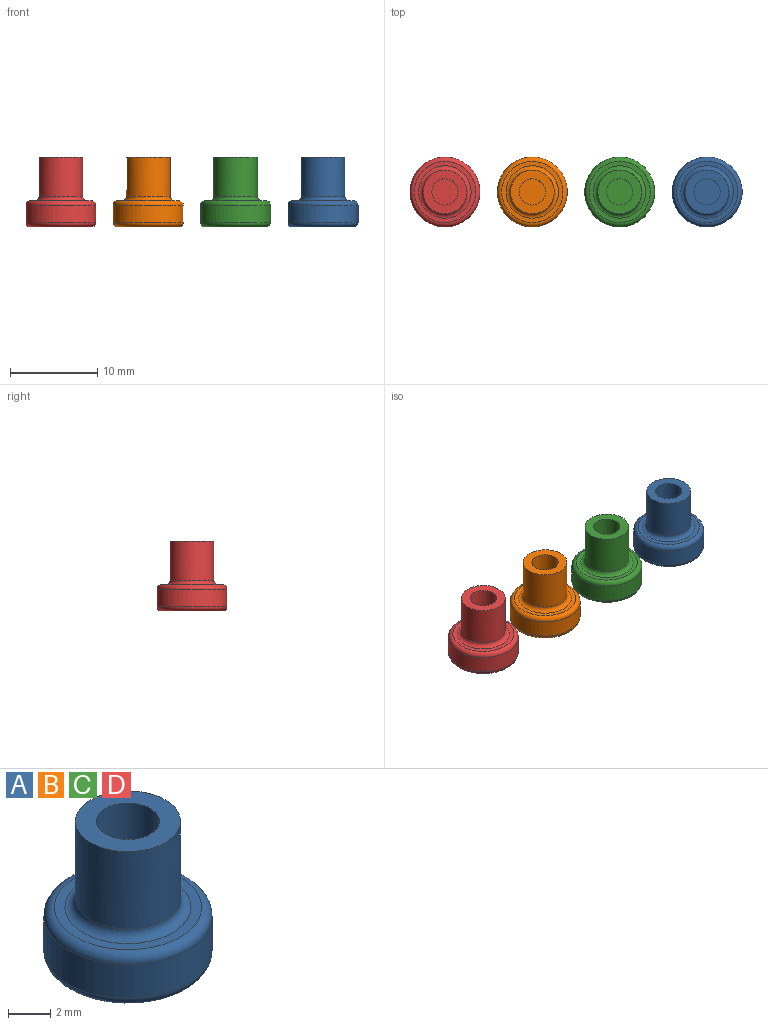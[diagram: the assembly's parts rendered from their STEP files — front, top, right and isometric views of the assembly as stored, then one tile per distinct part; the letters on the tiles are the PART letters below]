
ASSEMBLY  parts=4 mates=3
PART A: 10 faces, bbox 8.7x8.7x8 mm
  f0: cylinder r=4mm len=8mm, axis (0,0,1), area 50.3mm2, adj f7,f9
  f1: plane 7x7mm, normal (0,0,-1), area 38.5mm2, adj f7
  f2: plane 3x3mm, normal (0,0,1), area 7.1mm2, adj f3
  f3: cylinder r=1.5mm len=4mm, axis (0,0,1), area 37.7mm2, adj f2,f4
  f4: plane 5x5mm, normal (0,0,1), area 12.6mm2, adj f3,f5
  f5: cylinder r=2.5mm len=5mm, axis (0,0,1), area 70.7mm2, adj f4,f8
  f6: plane 7x7mm, normal (0,0,1), area 10.2mm2, adj f8,f9
  f7: torus R=3.5mm, axis (0,0,-1), area 18.8mm2, adj f0,f1
  f8: torus R=3mm, axis (0,0,-1), area 13.2mm2, adj f5,f6
  f9: torus R=3.5mm, axis (0,0,-1), area 18.8mm2, adj f0,f6
PART B: same geometry as A
PART C: same geometry as A
PART D: same geometry as A
PLACE A t=(30,0,3)mm
PLACE B t=(10,0,3)mm
PLACE C t=(20,0,3)mm
PLACE D t=(0,0,3)mm fixed
MATE fastened A.f9 <-> D.f1  axis (0,0,-1) through (30,0,0)mm
MATE fastened C.f9 <-> D.f1  axis (0,0,-1) through (20,0,0)mm
MATE fastened B.f9 <-> D.f1  axis (0,0,-1) through (10,0,0)mm
